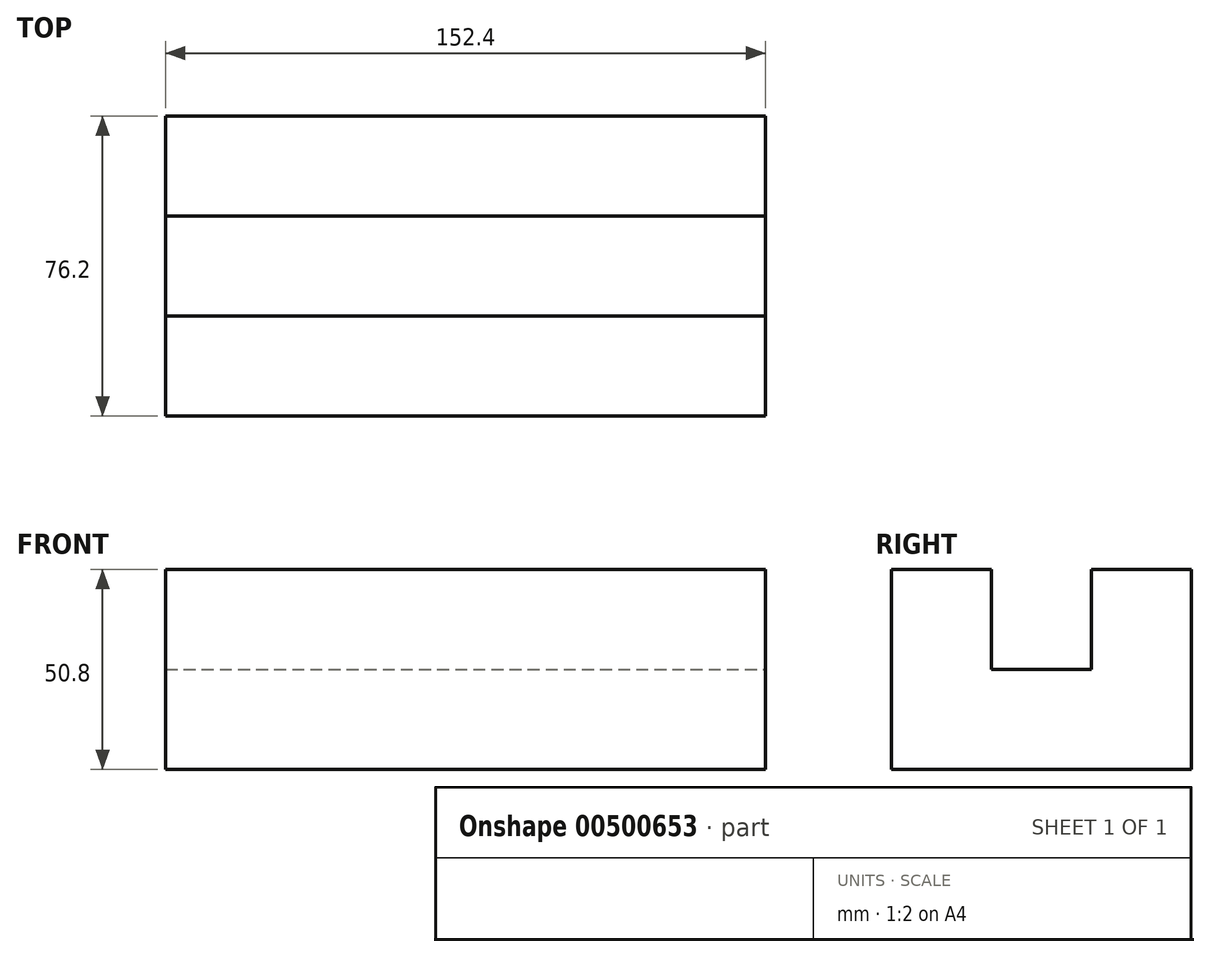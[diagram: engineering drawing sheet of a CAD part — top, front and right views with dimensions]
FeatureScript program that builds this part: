
annotation { "Feature Type Name" : "Feature", "Feature Type Description" : "" }
export const myFeature = defineFeature(function(context is Context, id is Id, definition is map)
    precondition{}
    {
        {
            var Q0;
            Q0=qCreatedBy(makeId("Top.planeOp"),FACE);
            var sketch = newSketch(context, id + "F0", { "sketchPlane" : qUnion([Q0])});
            skLineSegment(sketch, "E0.bottom", {"start": v(-35.82, 12.33) * mm, "end": v(116.58, 12.33) * mm});
            skLineSegment(sketch, "E0.top", {"start": v(-35.82, -13.07) * mm, "end": v(116.58, -13.07) * mm});
            skLineSegment(sketch, "E0.left", {"start": v(-35.82, 12.33) * mm, "end": v(-35.82, -13.07) * mm});
            skLineSegment(sketch, "E0.right", {"start": v(116.58, 12.33) * mm, "end": v(116.58, -13.07) * mm});
            skLineSegment(sketch, "E1.top", {"start": v(-35.82, -38.47) * mm, "end": v(116.58, -38.47) * mm});
            skLineSegment(sketch, "E1.left", {"start": v(-35.82, -13.07) * mm, "end": v(-35.82, -38.47) * mm});
            skLineSegment(sketch, "E1.right", {"start": v(116.58, -13.07) * mm, "end": v(116.58, -38.47) * mm});
            skLineSegment(sketch, "E2.bottom", {"start": v(-35.82, 37.73) * mm, "end": v(116.58, 37.73) * mm});
            skLineSegment(sketch, "E2.left", {"start": v(-35.82, 37.73) * mm, "end": v(-35.82, 12.33) * mm});
            skLineSegment(sketch, "E2.right", {"start": v(116.58, 37.73) * mm, "end": v(116.58, 12.33) * mm});
            skSolve(sketch);
        }
        {
            var Q0;
            Q0=makeQuery(id+"F0.imprint","IMPRINT",FACE,{"disambiguationData":[TD([[makeQuery(id+"F0.imprint","IMPRINT",EDGE,{"derivedFrom":sQuery(id+"F0.wireOp",EDGE,"E2.bottom")}),-1.0]])]});
            extrude(context, id + "F1", {"entities" : qUnion([Q0]), "depth" : 50.8 * mm});
        }
        {
            var Q0;
            Q0=makeQuery(id+"F0.imprint","IMPRINT",FACE,{"disambiguationData":[TD([[makeQuery(id+"F0.imprint","IMPRINT",EDGE,{"derivedFrom":sQuery(id+"F0.wireOp",EDGE,"E0.left")}),1.0]])]});
            extrude(context, id + "F2", {"entities" : qUnion([Q0]), "operationType" : NewBodyOperationType.ADD, "depth" : 25.4 * mm});
        }
        {
            var Q0;
            Q0=makeQuery(id+"F0.imprint","IMPRINT",FACE,{"disambiguationData":[TD([[makeQuery(id+"F0.imprint","IMPRINT",EDGE,{"derivedFrom":sQuery(id+"F0.wireOp",EDGE,"E0.top")}),-1.0]])]});
            extrude(context, id + "F3", {"entities" : qUnion([Q0]), "operationType" : NewBodyOperationType.ADD, "depth" : 50.8 * mm});
        }
    });
